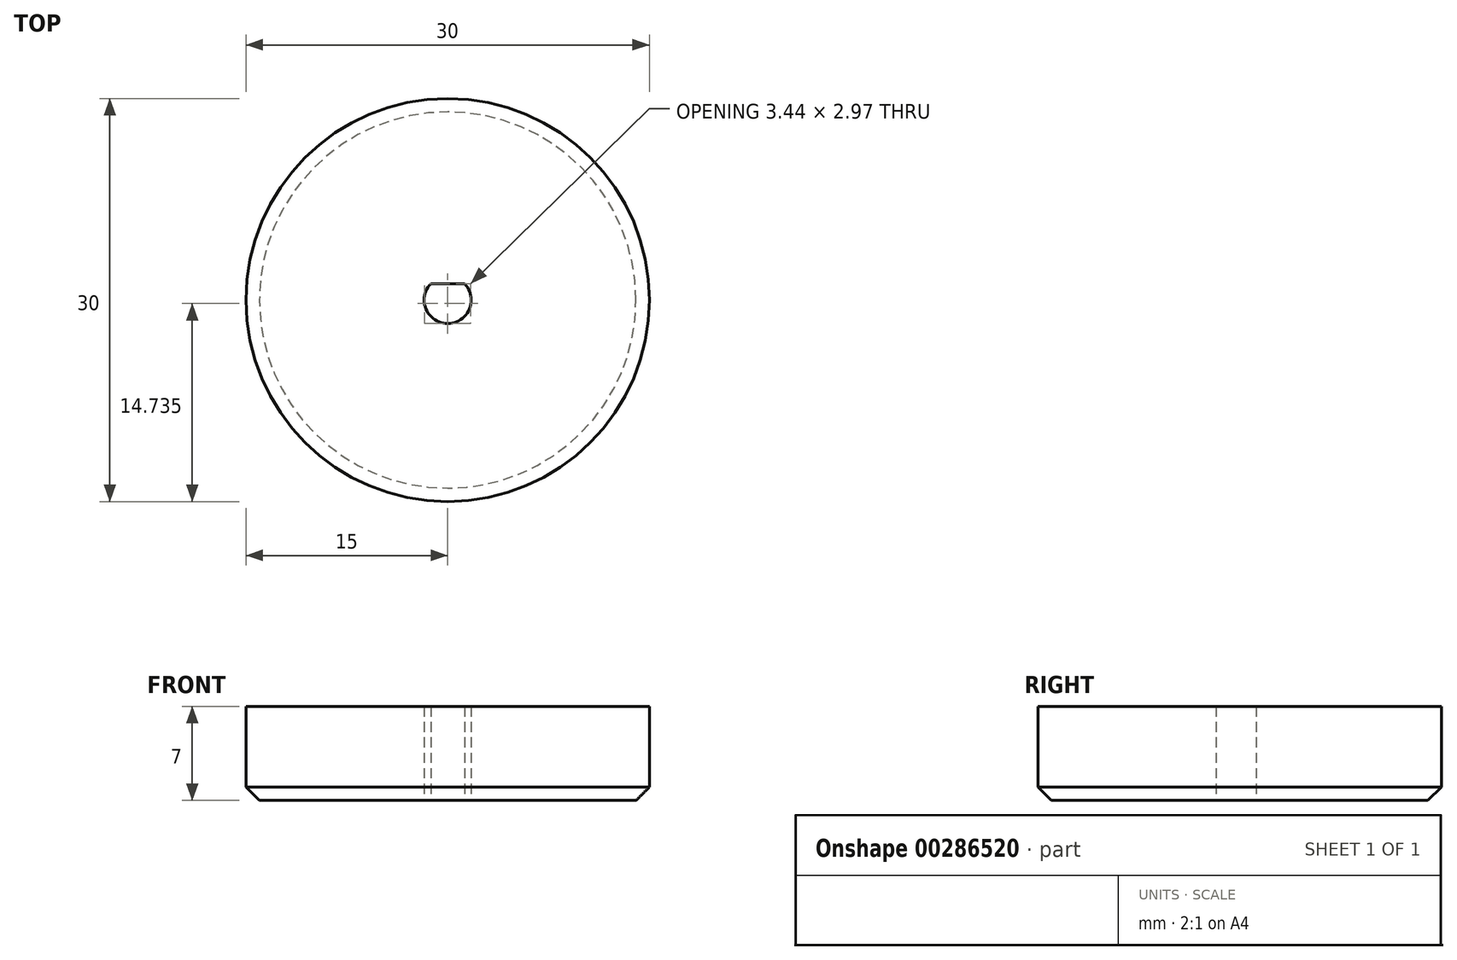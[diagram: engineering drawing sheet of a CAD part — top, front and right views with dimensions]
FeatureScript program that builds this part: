
annotation { "Feature Type Name" : "Feature", "Feature Type Description" : "" }
export const myFeature = defineFeature(function(context is Context, id is Id, definition is map)
    precondition{}
    {
        {
            var Q0;
            Q0=qCreatedBy(makeId("Top.planeOp"),FACE);
            var sketch = newSketch(context, id + "F0", { "sketchPlane" : qUnion([Q0])});
            skArc(sketch, "E0", {"start": v(-1.14, 0.97) * mm, "mid": v(0, -1.5) * mm, "end": v(1.14, 0.97) * mm});
            skLineSegment(sketch, "E1", {"start": v(-1.14, 0.97) * mm, "end": v(1.14, 0.97) * mm});
            skArc(sketch, "E2.0", {"start": v(-1.25, 1.22) * mm, "mid": v(0, -1.75) * mm, "end": v(1.25, 1.22) * mm});
            skLineSegment(sketch, "E2.1", {"start": v(-1.25, 1.22) * mm, "end": v(1.25, 1.22) * mm});
            skCircle(sketch, "E3", {"center": v(0, 0) * mm, "radius": 15 * mm});
            skSolve(sketch);
        }
        {
            var Q0;
            Q0=qSketchRegion(id+"F0",true);
            extrude(context, id + "F1", {"entities" : qUnion([Q0]), "depth" : 7 * mm, "offsetDistance" : 25 * mm});
        }
        {
            var Q0;
            Q0 = qSketchRegion(id + "F0", true);
            extrude(context, id + "F2", {"entities" : qUnion([Q0]), "operationType" : NewBodyOperationType.ADD, "depth" : 5 * mm, "offsetDistance" : 25 * mm});
        }
        {
            var Q0;
            Q0=makeQuery(id+"F1.opExtrude","CAP_EDGE",EDGE,{"disambiguationData":[OSD([sQuery(id+"F0.wireOp",EDGE,"E3")])],"isStart":true});
            chamfer(context, id + "F3", {"entities" : qUnion([Q0]), "width" : 1 * mm, "tangentPropagation" : true});
        }
    });
